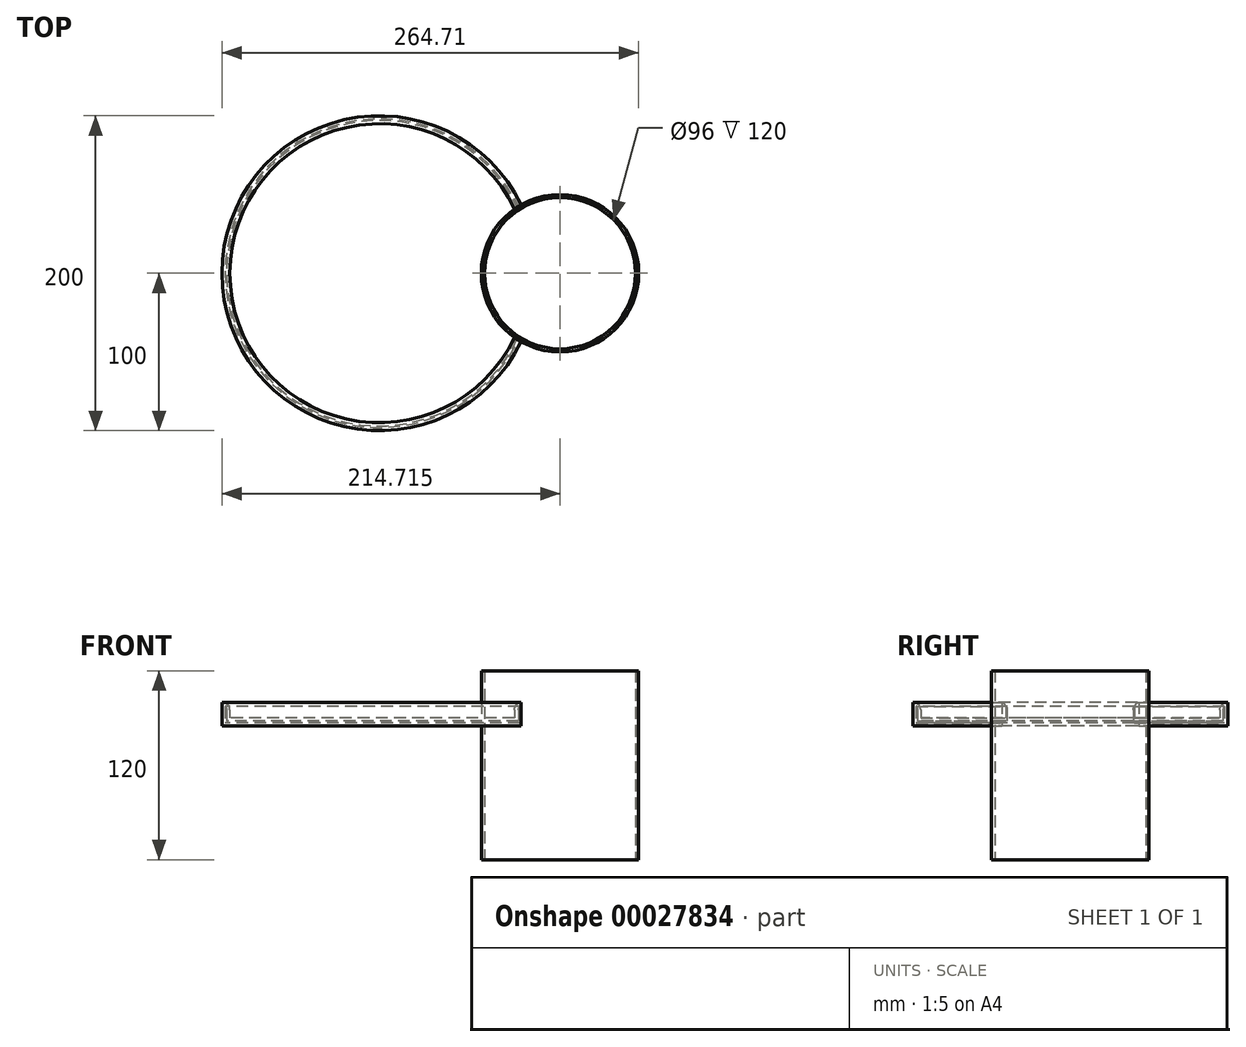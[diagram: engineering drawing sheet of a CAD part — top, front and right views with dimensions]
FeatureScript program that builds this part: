
annotation { "Feature Type Name" : "Feature", "Feature Type Description" : "" }
export const myFeature = defineFeature(function(context is Context, id is Id, definition is map)
    precondition{}
    {
        {
            var Q0;
            Q0=qCreatedBy(makeId("Top.planeOp"),FACE);
            var sketch = newSketch(context, id + "F0", { "sketchPlane" : qUnion([Q0])});
            skCircle(sketch, "E0", {"center": v(0, 0) * mm, "radius": 100 * mm});
            skSolve(sketch);
        }
        {
            var Q0;
            Q0=makeQuery(id+"F0.imprint","IMPRINT",FACE,{"disambiguationData":[TD([[makeQuery(id+"F0.imprint","IMPRINT",EDGE,{"derivedFrom":sQuery(id+"F0.wireOp",EDGE,"E0")}),1.0]])]});
            extrude(context, id + "F1", {"entities" : qUnion([Q0]), "depth" : 15 * mm});
        }
        {
            var Q0;
            Q0=makeQuery(id+"F1.opExtrude","CAP_FACE",FACE,{"disambiguationData":[OSD([sQuery(id+"F0.wireOp",EDGE,"E0")])],"isStart":false});
            shell(context, id + "F2", {"entities" : qUnion([Q0]), "thickness" : 5 * mm});
        }
        {
            var Q0;
            {var subQ0=sQuery(id+"F0.wireOp",EDGE,"E0");Q0=makeQuery(id+"F2.opShell","OFFSET_EDGE",EDGE,{"disambiguationData":[OSD([subQ0]),TDD([makeQuery(id+"F1.opExtrude","CAP_EDGE",EDGE,{"disambiguationData":[OSD([subQ0])],"isStart":false})])]});}
            fillet(context, id + "F3", {"entities" : qUnion([Q0]), "radius" : 5 * mm, "allowEdgeOverflow" : false});
        }
        {
            var Q0;
            Q0=qCreatedBy(makeId("Top.planeOp"),FACE);
            var sketch = newSketch(context, id + "F4", { "sketchPlane" : qUnion([Q0])});
            skCircle(sketch, "E1", {"center": v(114.71, 0) * mm, "radius": 50 * mm});
            skSolve(sketch);
        }
        {
            var Q0;
            Q0=makeQuery(id+"F4.imprint","IMPRINT",FACE,{"disambiguationData":[TD([[makeQuery(id+"F4.imprint","IMPRINT",EDGE,{"derivedFrom":sQuery(id+"F4.wireOp",EDGE,"E1")}),1.0]])]});
            extrude(context, id + "F5", {"entities" : qUnion([Q0]), "operationType" : NewBodyOperationType.ADD, "endBound" : BoundingType.SYMMETRIC, "depth" : 70 * mm});
        }
        {
            var Q0;
            Q0=makeQuery(id+"F5.opExtrude","CAP_FACE",FACE,{"disambiguationData":[OSD([sQuery(id+"F4.wireOp",EDGE,"E1")])],"isStart":true});
            var Q1;
            Q1=makeQuery(id+"F5.opExtrude","CAP_FACE",FACE,{"disambiguationData":[OSD([sQuery(id+"F4.wireOp",EDGE,"E1")])],"isStart":false});
            var Q2;
            Q2=makeQuery(id+"F1.opExtrude","SWEPT_BODY",BODY,{"disambiguationData":[OSD([sQuery(id+"F0.wireOp",EDGE,"E0")])]});
            shell(context, id + "F6", {"entities" : qUnion([Q0, Q1]), "parts" : qUnion([Q2]), "thickness" : 2 * mm});
        }
        {
            var Q0;
            Q0=makeQuery(id+"F5.opExtrude","CAP_FACE",FACE,{"disambiguationData":[OSD([sQuery(id+"F4.wireOp",EDGE,"E1")])],"isStart":true});
            var sketch = newSketch(context, id + "F7", { "sketchPlane" : qUnion([Q0])});
            skPoint(sketch, "E2", {"position": v(114.71, 0) * mm});
            skCircle(sketch, "E3", {"center": v(114.71, 0) * mm, "radius": 50 * mm});
            skSolve(sketch);
        }
        {
            var Q0;
            Q0=makeQuery(id+"F7.imprint","IMPRINT",FACE,{"disambiguationData":[TD([[makeQuery(id+"F7.imprint","IMPRINT",EDGE,{"derivedFrom":sQuery(id+"F7.wireOp",EDGE,"E3")}),-1.0]])]});
            extrude(context, id + "F8", {"entities" : qUnion([Q0]), "operationType" : NewBodyOperationType.ADD, "depth" : 50 * mm});
        }
    });
